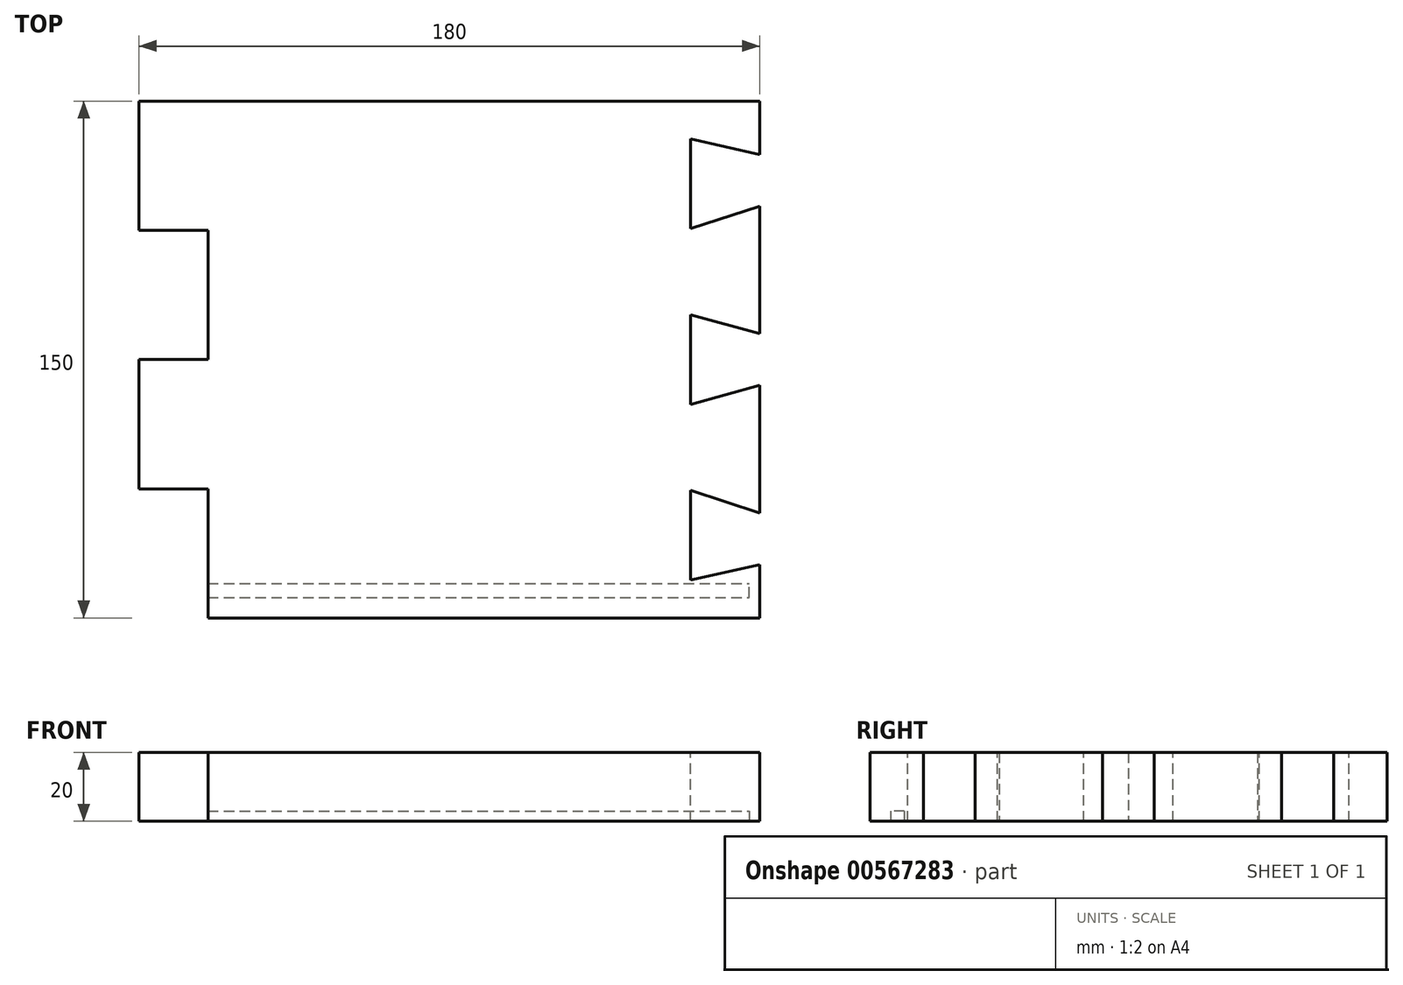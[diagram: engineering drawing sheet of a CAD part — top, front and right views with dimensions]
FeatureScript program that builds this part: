
annotation { "Feature Type Name" : "Feature", "Feature Type Description" : "" }
export const myFeature = defineFeature(function(context is Context, id is Id, definition is map)
    precondition{}
    {
        {
            var Q0;
            Q0=qCreatedBy(makeId("Top.planeOp"),FACE);
            var sketch = newSketch(context, id + "F0", { "sketchPlane" : qUnion([Q0])});
            skLineSegment(sketch, "E0.bottom", {"start": v(-180, 187.5) * mm, "end": v(0, 187.5) * mm});
            skLineSegment(sketch, "E0.top", {"start": v(-160, 37.5) * mm, "end": v(0, 37.5) * mm});
            skLineSegment(sketch, "E0.left", {"start": v(-180, 187.5) * mm, "end": v(-180, 150) * mm});
            skLineSegment(sketch, "E0.right", {"start": v(0, 187.5) * mm, "end": v(0, 37.5) * mm});
            skLineSegment(sketch, "E1", {"start": v(-160, 150) * mm, "end": v(-160, 112.5) * mm});
            skLineSegment(sketch, "E2", {"start": v(-160, 112.5) * mm, "end": v(-180, 112.5) * mm});
            skLineSegment(sketch, "E3", {"start": v(-180, 150) * mm, "end": v(-160, 150) * mm});
            skLineSegment(sketch, "E4", {"start": v(-180, 75) * mm, "end": v(-160, 75) * mm});
            skLineSegment(sketch, "E5.trimOffspring", {"start": v(-160, 75) * mm, "end": v(-160, 37.5) * mm});
            skLineSegment(sketch, "E6.trimOffspring", {"start": v(-180, 112.5) * mm, "end": v(-180, 75) * mm});
            skPoint(sketch, "E7.orphan", {"position": v(-180, 37.5) * mm});
            skSolve(sketch);
        }
        {
            var Q0;
            Q0=makeQuery(id+"F0.imprint","IMPRINT",FACE,{"disambiguationData":[TD([[makeQuery(id+"F0.imprint","IMPRINT",EDGE,{"derivedFrom":sQuery(id+"F0.wireOp",EDGE,"E0.bottom")}),-1.0]])]});
            extrude(context, id + "F1", {"entities" : qUnion([Q0]), "depth" : 20 * mm, "offsetDistance" : 25 * mm});
        }
        {
            var Q0;
            Q0=makeQuery(id+"F1.opExtrude","CAP_FACE",FACE,{"disambiguationData":[OSD([sQuery(id+"F0.wireOp",EDGE,"E0.bottom"),sQuery(id+"F0.wireOp",EDGE,"E0.top"),sQuery(id+"F0.wireOp",EDGE,"E0.left"),sQuery(id+"F0.wireOp",EDGE,"E0.right"),sQuery(id+"F0.wireOp",EDGE,"E1"),sQuery(id+"F0.wireOp",EDGE,"E2"),sQuery(id+"F0.wireOp",EDGE,"E3"),sQuery(id+"F0.wireOp",EDGE,"E4"),sQuery(id+"F0.wireOp",EDGE,"E5.trimOffspring"),sQuery(id+"F0.wireOp",EDGE,"E6.trimOffspring")])],"isStart":false});
            var sketch = newSketch(context, id + "F2", { "sketchPlane" : qUnion([Q0])});
            skLineSegment(sketch, "E8", {"start": v(-20, 187.5) * mm, "end": v(-20, 37.5) * mm});
            skLineSegment(sketch, "E9", {"start": v(-20, 176.5) * mm, "end": v(0, 172) * mm});
            skLineSegment(sketch, "E10", {"start": v(-20, 150.5) * mm, "end": v(0, 157) * mm});
            skLineSegment(sketch, "E11", {"start": v(-20, 125.5) * mm, "end": v(0, 120) * mm});
            skLineSegment(sketch, "E12", {"start": v(-20, 99.5) * mm, "end": v(0, 105) * mm});
            skLineSegment(sketch, "E13", {"start": v(-20, 74.5) * mm, "end": v(0, 68) * mm});
            skLineSegment(sketch, "E14", {"start": v(-20, 48.5) * mm, "end": v(0, 53) * mm});
            skPoint(sketch, "E15.orphan", {"position": v(-16.16, 100.55) * mm});
            skSolve(sketch);
        }
        {
            var Q0;
            {var subQ0=sQuery(id+"F2.wireOp",EDGE,"E9");Q0=makeQuery(id+"F2.imprint","IMPRINT",FACE,{"disambiguationData":[TD([[makeQuery(id+"F2.imprint","IMPRINT",EDGE,{"derivedFrom":subQ0}),-1.0]])]});}
            var Q1;
            {var subQ0=sQuery(id+"F2.wireOp",EDGE,"E11");Q1=makeQuery(id+"F2.imprint","IMPRINT",FACE,{"disambiguationData":[TD([[makeQuery(id+"F2.imprint","IMPRINT",EDGE,{"derivedFrom":subQ0}),-1.0]])]});}
            var Q2;
            {var subQ0=sQuery(id+"F2.wireOp",EDGE,"E13");Q2=makeQuery(id+"F2.imprint","IMPRINT",FACE,{"disambiguationData":[TD([[makeQuery(id+"F2.imprint","IMPRINT",EDGE,{"derivedFrom":subQ0}),-1.0]])]});}
            extrude(context, id + "F3", {"entities" : qUnion([Q0, Q1, Q2]), "operationType" : NewBodyOperationType.REMOVE, "oppositeDirection" : true, "depth" : 20 * mm, "offsetDistance" : 25 * mm});
        }
        {
            var Q0;
            Q0=makeQuery(id+"F1.opExtrude","CAP_FACE",FACE,{"disambiguationData":[OSD([sQuery(id+"F0.wireOp",EDGE,"E0.bottom"),sQuery(id+"F0.wireOp",EDGE,"E0.top"),sQuery(id+"F0.wireOp",EDGE,"E0.left"),sQuery(id+"F0.wireOp",EDGE,"E0.right"),sQuery(id+"F0.wireOp",EDGE,"E1"),sQuery(id+"F0.wireOp",EDGE,"E2"),sQuery(id+"F0.wireOp",EDGE,"E3"),sQuery(id+"F0.wireOp",EDGE,"E4"),sQuery(id+"F0.wireOp",EDGE,"E5.trimOffspring"),sQuery(id+"F0.wireOp",EDGE,"E6.trimOffspring")])],"isStart":true});
            var sketch = newSketch(context, id + "F4", { "sketchPlane" : qUnion([Q0])});
            skLineSegment(sketch, "E16", {"start": v(-160, -47.5) * mm, "end": v(-3, -47.5) * mm});
            skLineSegment(sketch, "E17", {"start": v(-160, -43.5) * mm, "end": v(-3, -43.5) * mm});
            skLineSegment(sketch, "E18", {"start": v(-3, -43.5) * mm, "end": v(-3, -47.5) * mm});
            skSolve(sketch);
        }
        {
            var Q0;
            {var subQ0=sQuery(id+"F4.wireOp",EDGE,"E16");Q0=makeQuery(id+"F4.imprint","IMPRINT",FACE,{"disambiguationData":[TD([[makeQuery(id+"F4.imprint","IMPRINT",EDGE,{"derivedFrom":subQ0}),1.0]])]});}
            extrude(context, id + "F5", {"entities" : qUnion([Q0]), "operationType" : NewBodyOperationType.REMOVE, "oppositeDirection" : true, "depth" : 3 * mm, "offsetDistance" : 25 * mm});
        }
    });
